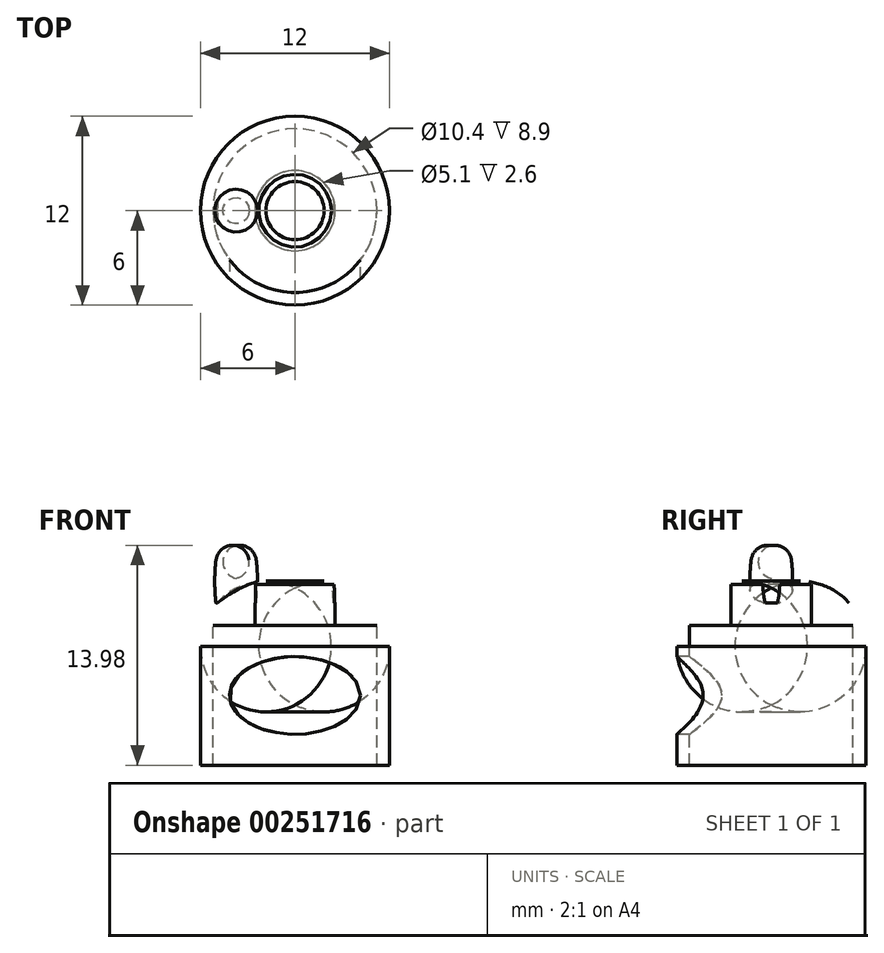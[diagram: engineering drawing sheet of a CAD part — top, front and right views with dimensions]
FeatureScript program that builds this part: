
annotation { "Feature Type Name" : "Feature", "Feature Type Description" : "" }
export const myFeature = defineFeature(function(context is Context, id is Id, definition is map)
    precondition{}
    {
        {
            var Q0;
            Q0=qCreatedBy(makeId("Front.planeOp"),FACE);
            var sketch = newSketch(context, id + "F0", { "sketchPlane" : qUnion([Q0])});
            skLineSegment(sketch, "E0", {"start": v(0, 12.38) * mm, "end": v(0, -2.2) * mm});
            skLineSegment(sketch, "E1", {"start": v(6, -1.32) * mm, "end": v(0, -1.32) * mm});
            skPoint(sketch, "E2.visualSharp", {"position": v(6, 8.38) * mm});
            skLineSegment(sketch, "E3", {"start": v(0, 8.38) * mm, "end": v(6, 8.38) * mm});
            skLineSegment(sketch, "E4", {"start": v(6, -1.32) * mm, "end": v(6, 8.38) * mm});
            skLineSegment(sketch, "E5", {"start": v(6, 8.38) * mm, "end": v(6, 10.38) * mm});
            skLineSegment(sketch, "E6", {"start": v(6, 10.38) * mm, "end": v(0, 10.38) * mm});
            skLineSegment(sketch, "E7", {"start": v(0, 10.18) * mm, "end": v(2.55, 10.18) * mm});
            skLineSegment(sketch, "E8", {"start": v(2.55, 10.18) * mm, "end": v(2.55, 8.38) * mm});
            skSolve(sketch);
        }
        {
            var Q0;
            {var subQ5=sQuery(id+"F0.wireOp",EDGE,"E1");Q0=makeQuery(id+"F0.imprint","IMPRINT",FACE,{"disambiguationData":[TD([[makeQuery(id+"F0.imprint","IMPRINT",EDGE,{"derivedFrom":subQ5}),-1.0]])]});}
            var Q1;
            Q1=sQuery(id+"F0.wireOp",EDGE,"E0");
            revolve(context, id + "F1", {"entities" : qUnion([Q0]), "axis" : qUnion([Q1]), "revolveType" : RevolveType.FULL});
        }
        {
            var Q0;
            {var subQ1=sQuery(id+"F0.wireOp",EDGE,"E5");Q0=makeQuery(id+"F0.imprint","IMPRINT",FACE,{"disambiguationData":[TD([[makeQuery(id+"F0.imprint","IMPRINT",EDGE,{"derivedFrom":subQ1}),1.0]])]});}
            var Q1;
            Q1=sQuery(id+"F0.wireOp",EDGE,"E0");
            revolve(context, id + "F2", {"entities" : qUnion([Q0]), "axis" : qUnion([Q1]), "revolveType" : RevolveType.FULL});
        }
        {
            var Q0;
            Q0=makeQuery(id+"F1.opRevolve","SWEPT_FACE",FACE,{"disambiguationData":[OSD([sQuery(id+"F0.wireOp",EDGE,"E1")])]});
            shell(context, id + "F3", {"entities" : qUnion([Q0]), "thickness" : 0.8 * mm});
        }
        {
            var Q0;
            Q0=makeQuery(id+"F1.opRevolve","SWEPT_FACE",FACE,{"disambiguationData":[OSD([sQuery(id+"F0.wireOp",EDGE,"E3")])]});
            var sketch = newSketch(context, id + "F4", { "sketchPlane" : qUnion([Q0])});
            skCircle(sketch, "E9.0.0", {"center": v(0, 0) * mm, "radius": 6 * mm, "construction": true});
            skCircle(sketch, "E10", {"center": v(0, 0) * mm, "radius": 2.55 * mm});
            skSolve(sketch);
        }
        {
            var Q0;
            Q0=makeQuery(id+"F4.imprint","IMPRINT",FACE,{"disambiguationData":[TD([[makeQuery(id+"F4.imprint","IMPRINT",EDGE,{"derivedFrom":sQuery(id+"F4.wireOp",EDGE,"E10")}),1.0]])]});
            extrude(context, id + "F5", {"entities" : qUnion([Q0]), "operationType" : NewBodyOperationType.REMOVE, "oppositeDirection" : true, "depth" : 25 * mm, "hasSecondDirection" : true, "secondDirectionOppositeDirection" : false, "secondDirectionDepth" : 1.8 * mm});
        }
        {
            var Q0;
            Q0=makeQuery(id+"F2.opRevolve","SWEPT_BODY",BODY,{"disambiguationData":[OSD([sQuery(id+"F0.wireOp",EDGE,"E0"),sQuery(id+"F0.wireOp",EDGE,"E3"),sQuery(id+"F0.wireOp",EDGE,"E5"),sQuery(id+"F0.wireOp",EDGE,"E6"),sQuery(id+"F0.wireOp",EDGE,"E7"),sQuery(id+"F0.wireOp",EDGE,"E8")])]});
            var Q1;
            Q1=makeQuery(id+"F1.opRevolve","SWEPT_BODY",BODY,{"disambiguationData":[OSD([sQuery(id+"F0.wireOp",EDGE,"E0"),sQuery(id+"F0.wireOp",EDGE,"E1"),sQuery(id+"F0.wireOp",EDGE,"E3"),sQuery(id+"F0.wireOp",EDGE,"E4")])]});
            booleanBodies(context, id + "F6", {"operationType" : BooleanOperationType.UNION, "tools" : qUnion([Q0, Q1])});
        }
        {
            var Q0;
            Q0=qCreatedBy(makeId("Front.planeOp"),FACE);
            var sketch = newSketch(context, id + "F7", { "sketchPlane" : qUnion([Q0])});
            skEllipse(sketch, "E11", {"center": v(0, 3.12) * mm, "majorRadius": 4.15 * mm, "minorRadius": 2.47 * mm, "majorAxis": v(1, 0)});
            skPoint(sketch, "E12", {"position": v(0, 0.65) * mm});
            skSolve(sketch);
        }
        {
            var Q0;
            Q0=makeQuery(id+"F7.imprint","IMPRINT",FACE,{"disambiguationData":[TD([[makeQuery(id+"F7.imprint","IMPRINT",EDGE,{"derivedFrom":sQuery(id+"F7.wireOp",EDGE,"E11")}),1.0]])]});
            extrude(context, id + "F8", {"entities" : qUnion([Q0]), "operationType" : NewBodyOperationType.REMOVE, "depth" : 25 * mm});
        }
        {
            var Q0;
            Q0=makeQuery(id+"F2.opRevolve","SWEPT_EDGE",EDGE,{"disambiguationData":[OSD([sQuery(id+"F0.wireOp",EDGE,"E5"),sQuery(id+"F0.wireOp",EDGE,"E6")])]});
            fillet(context, id + "F9", {"entities" : qUnion([Q0]), "radius" : 4.15 * mm, "tangentPropagation" : true, "allowEdgeOverflow" : false});
        }
        {
            var Q0;
            Q0=qCreatedBy(makeId("Top.planeOp"),FACE);
            cPlane(context, id + "F10", {"entities" : qUnion([Q0]), "cplaneType" : CPlaneType.OFFSET, "offset" : 9 * mm, "width" : 150 * mm, "height" : 150 * mm});
        }
        {
            var Q0;
            Q0=qCreatedBy(id+"F10.planeOp",FACE);
            var sketch = newSketch(context, id + "F11", { "sketchPlane" : qUnion([Q0])});
            skLineSegment(sketch, "E13.0.4", {"start": v(-2.93, 0) * mm, "end": v(-2.95, 0) * mm});
            skCircle(sketch, "E14", {"center": v(-3.74, 0) * mm, "radius": 1.28 * mm});
            skSolve(sketch);
        }
        {
            var Q0;
            Q0=qCreatedBy(makeId("Front.planeOp"),FACE);
            var sketch = newSketch(context, id + "F12", { "sketchPlane" : qUnion([Q0])});
            skPoint(sketch, "E15.0", {"position": v(-3.74, 9) * mm});
            skLineSegment(sketch, "E16.0", {"start": v(-5.02, 9) * mm, "end": v(-2.46, 9) * mm});
            skLineSegment(sketch, "E17", {"start": v(-3.74, 9) * mm, "end": v(-3.74, 15.06) * mm});
            skArc(sketch, "E18", {"start": v(-2.46, 11.72) * mm, "mid": v(-2.9, 12.46) * mm, "end": v(-3.74, 12.63) * mm});
            skArc(sketch, "E19", {"start": v(-2.46, 9) * mm, "mid": v(-2.38, 10.36) * mm, "end": v(-2.46, 11.72) * mm});
            skSolve(sketch);
        }
        {
            var Q0;
            {var subQ4=sQuery(id+"F12.wireOp",EDGE,"E18");Q0=makeQuery(id+"F12.imprint","IMPRINT",FACE,{"disambiguationData":[TD([[makeQuery(id+"F12.imprint","IMPRINT",EDGE,{"derivedFrom":subQ4}),1.0]])]});}
            var Q1;
            Q1=sQuery(id+"F12.wireOp",EDGE,"E17");
            revolve(context, id + "F13", {"entities" : qUnion([Q0]), "axis" : qUnion([Q1]), "revolveType" : RevolveType.FULL});
        }
        {
            var Q0;
            Q0=makeQuery(id+"F13.opRevolve","SWEPT_BODY",BODY,{"disambiguationData":[OSD([sQuery(id+"F12.wireOp",EDGE,"E16.0"),sQuery(id+"F12.wireOp",EDGE,"E17"),sQuery(id+"F12.wireOp",EDGE,"E18"),sQuery(id+"F12.wireOp",EDGE,"E19")])]});
            var Q1;
            Q1=qCreatedBy(makeId("Right.planeOp"),FACE);
            mirror(context, id + "F14", {"operationType" : NewBodyOperationType.ADD, "entities" : qUnion([Q0]), "mirrorPlane" : qUnion([Q1])});
        }
        {
            var Q0;
            {var subQ4=sQuery(id+"F12.wireOp",EDGE,"E18");Q0=makeQuery(id+"F12.imprint","IMPRINT",FACE,{"disambiguationData":[TD([[makeQuery(id+"F12.imprint","IMPRINT",EDGE,{"derivedFrom":subQ4}),1.0]])]});}
            var Q1;
            Q1=sQuery(id+"F12.wireOp",EDGE,"E17");
            revolve(context, id + "F15", {"operationType" : NewBodyOperationType.ADD, "entities" : qUnion([Q0]), "axis" : qUnion([Q1]), "revolveType" : RevolveType.FULL});
        }
    });
